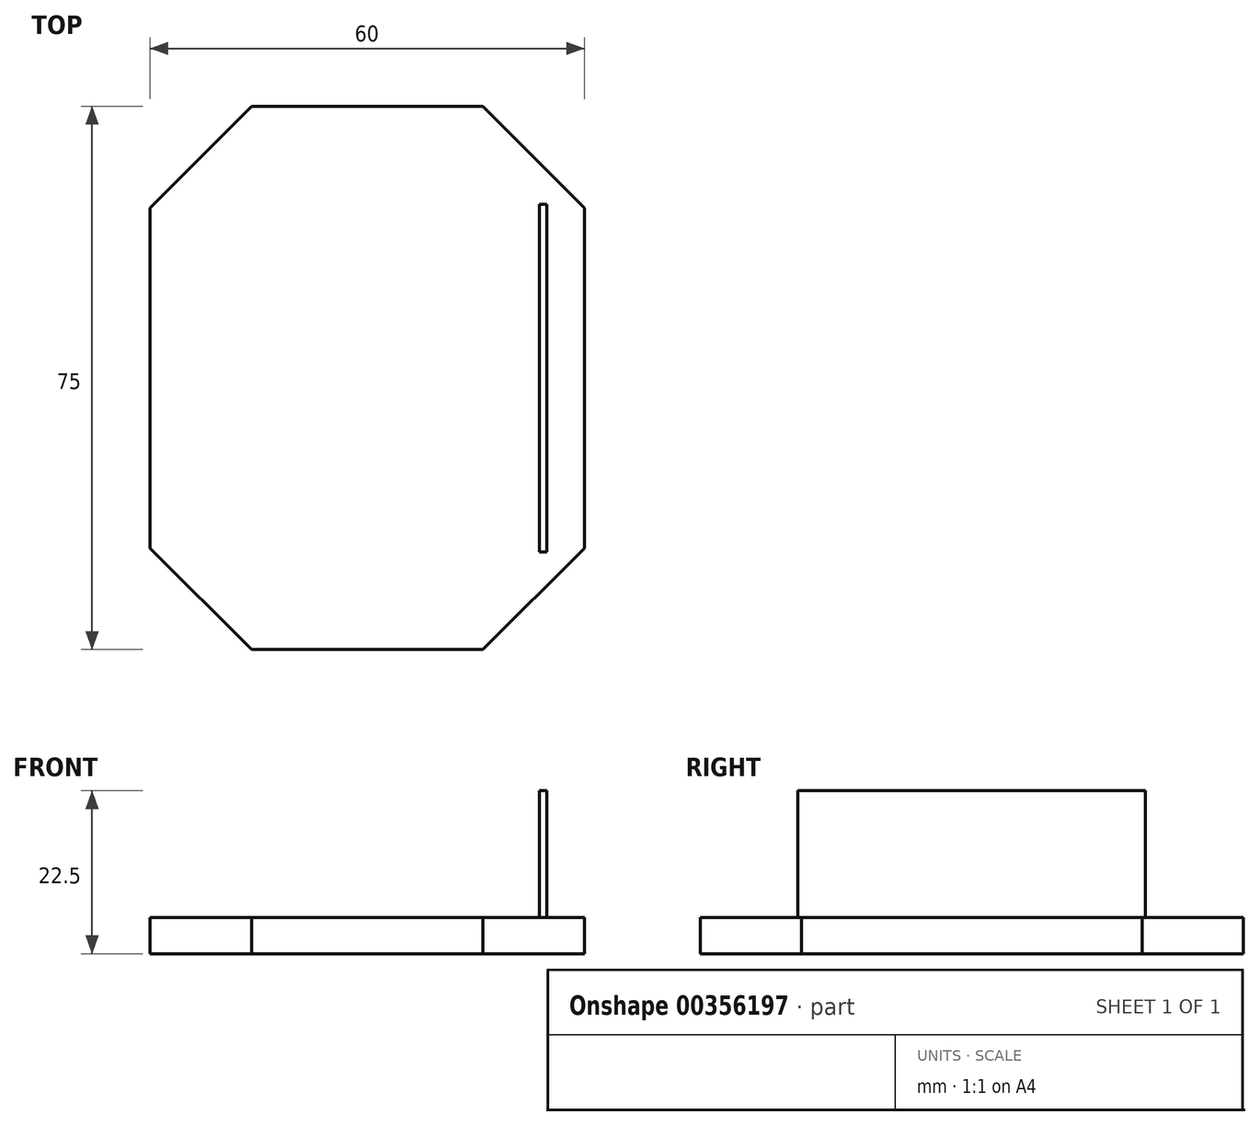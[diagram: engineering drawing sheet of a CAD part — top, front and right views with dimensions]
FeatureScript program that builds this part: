
annotation { "Feature Type Name" : "Feature", "Feature Type Description" : "" }
export const myFeature = defineFeature(function(context is Context, id is Id, definition is map)
    precondition{}
    {
        {
            var Q0;
            Q0=qCreatedBy(makeId("Top.planeOp"),FACE);
            var sketch = newSketch(context, id + "F0", { "sketchPlane" : qUnion([Q0])});
            skPoint(sketch, "E0", {"position": v(-30, 28.5) * mm});
            skPoint(sketch, "E1", {"position": v(-21, 37.5) * mm});
            skPoint(sketch, "E2", {"position": v(21, 37.5) * mm});
            skPoint(sketch, "E3", {"position": v(30, 28.5) * mm});
            skPoint(sketch, "E4", {"position": v(-30, -28.5) * mm});
            skPoint(sketch, "E5", {"position": v(-21, -37.5) * mm});
            skPoint(sketch, "E6", {"position": v(21, -37.5) * mm});
            skPoint(sketch, "E7", {"position": v(30, -28.5) * mm});
            skPoint(sketch, "E8", {"position": v(16, 37.5) * mm});
            skPoint(sketch, "E9", {"position": v(30, 23.5) * mm});
            skPoint(sketch, "E10", {"position": v(-16, 37.5) * mm});
            skPoint(sketch, "E11", {"position": v(-30, 23.5) * mm});
            skPoint(sketch, "E12", {"position": v(-30, -23.5) * mm});
            skPoint(sketch, "E13", {"position": v(-16, -37.5) * mm});
            skPoint(sketch, "E14", {"position": v(16, -37.5) * mm});
            skPoint(sketch, "E15", {"position": v(30, -23.5) * mm});
            skLineSegment(sketch, "E16", {"start": v(16, -37.5) * mm, "end": v(30, -23.5) * mm});
            skLineSegment(sketch, "E17", {"start": v(-16, -37.5) * mm, "end": v(-30, -23.5) * mm});
            skLineSegment(sketch, "E18", {"start": v(-30, 23.5) * mm, "end": v(-16, 37.5) * mm});
            skLineSegment(sketch, "E19", {"start": v(16, 37.5) * mm, "end": v(30, 23.5) * mm});
            skLineSegment(sketch, "E20", {"start": v(-16, 37.5) * mm, "end": v(16, 37.5) * mm});
            skLineSegment(sketch, "E21", {"start": v(30, 23.5) * mm, "end": v(30, -23.5) * mm});
            skLineSegment(sketch, "E22", {"start": v(16, -37.5) * mm, "end": v(-16, -37.5) * mm});
            skLineSegment(sketch, "E23", {"start": v(-30, -23.5) * mm, "end": v(-30, 23.5) * mm});
            skSolve(sketch);
        }
        {
            var Q0;
            Q0 = qSketchRegion(id + "F0", true);
            extrude(context, id + "F1", {"entities" : qUnion([Q0]), "depth" : 5 * mm, "offsetDistance" : 25 * mm});
        }
        {
            var Q0;
            Q0=makeQuery(id+"F1.opExtrude","CAP_FACE",FACE,{"disambiguationData":[OSD([sQuery(id+"F0.wireOp",EDGE,"E16"),sQuery(id+"F0.wireOp",EDGE,"E17"),sQuery(id+"F0.wireOp",EDGE,"E18"),sQuery(id+"F0.wireOp",EDGE,"E19"),sQuery(id+"F0.wireOp",EDGE,"E20"),sQuery(id+"F0.wireOp",EDGE,"E21"),sQuery(id+"F0.wireOp",EDGE,"E22"),sQuery(id+"F0.wireOp",EDGE,"E23")])],"isStart":false});
            var sketch = newSketch(context, id + "F2", { "sketchPlane" : qUnion([Q0])});
            skPoint(sketch, "E24", {"position": v(30, 0) * mm});
            skPoint(sketch, "E25", {"position": v(24.8, 0) * mm});
            skLineSegment(sketch, "E26", {"start": v(24.8, 0) * mm, "end": v(24.8, -24) * mm});
            skLineSegment(sketch, "E27", {"start": v(24.8, -24) * mm, "end": v(24.8, 24) * mm});
            skLineSegment(sketch, "E28", {"start": v(24.8, 24) * mm, "end": v(23.8, 24) * mm});
            skLineSegment(sketch, "E29", {"start": v(23.8, 24) * mm, "end": v(23.8, -24) * mm});
            skLineSegment(sketch, "E30", {"start": v(23.8, -24) * mm, "end": v(24.8, -24) * mm});
            skPoint(sketch, "E31", {"position": v(-2, 24) * mm});
            skCircle(sketch, "E32", {"center": v(-2, 30) * mm, "radius": 2 * mm});
            skPoint(sketch, "E33", {"position": v(-25, 24) * mm});
            skPoint(sketch, "E34", {"position": v(-25, -0.5) * mm});
            skCircle(sketch, "E35", {"center": v(-25, -0.5) * mm, "radius": 1.25 * mm});
            skCircle(sketch, "E36", {"center": v(-12.2, -31) * mm, "radius": 2 * mm});
            skCircle(sketch, "E37", {"center": v(7.8, -31) * mm, "radius": 2 * mm});
            skSolve(sketch);
        }
        {
            var Q0;
            {var subQ0=sQuery(id+"F2.wireOp",EDGE,"E28");Q0=makeQuery(id+"F2.imprint","IMPRINT",FACE,{"disambiguationData":[TD([[makeQuery(id+"F2.imprint","IMPRINT",EDGE,{"derivedFrom":subQ0}),1.0]])]});}
            extrude(context, id + "F3", {"entities" : qUnion([Q0]), "operationType" : NewBodyOperationType.ADD, "depth" : 17.5 * mm, "offsetDistance" : 25 * mm});
        }
    });
